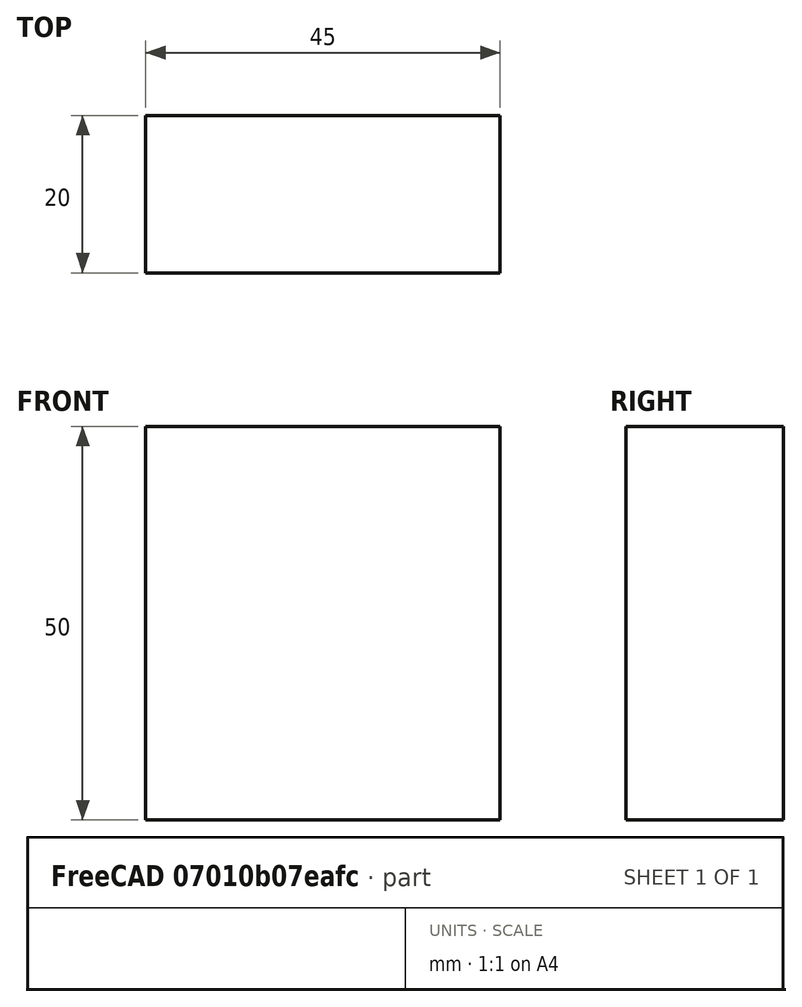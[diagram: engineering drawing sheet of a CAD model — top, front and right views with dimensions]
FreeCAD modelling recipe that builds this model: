
FCSTD DOCUMENT  (FreeCAD 0.15R4671 (Git))
Label: Flat Bar 45x20 EN10058 S235JR
License: All rights reserved
LicenseURL: http://en.wikipedia.org/wiki/All_rights_reserved
objects: Sketcher::SketchObject×1, Part::Extrusion×1
note: 2 computed .brp shape members not serialized (recipe doc carries the construction recipe); baked Part::Feature solids carry a one-line shape summary decoded from their .brp

FEATURE [Sketcher::SketchObject] Sketch
  sketch-geometry (4):
    g0: LineSegment StartX=-22.5 StartY=-10 StartZ=0 EndX=22.5 EndY=-10 EndZ=0
    g1: LineSegment StartX=22.5 StartY=-10 StartZ=0 EndX=22.5 EndY=10 EndZ=0
    g2: LineSegment StartX=22.5 StartY=10 StartZ=0 EndX=-22.5 EndY=10 EndZ=0
    g3: LineSegment StartX=-22.5 StartY=10 StartZ=0 EndX=-22.5 EndY=-10 EndZ=0
  constraints (12):
    c: Coincident(g0,g1)
    c: Coincident(g1,g2)
    c: Coincident(g2,g3)
    c: Coincident(g3,g0)
    c: Horizontal(g0)
    c: Horizontal(g2)
    c: Vertical(g1)
    c: Vertical(g3)
    c: Symmetric(g1,g2,g-2)
    c: Symmetric(g0,g1,g-1)
    c: DistanceY(g1) = 20
    c: DistanceX(g0) = 45
FEATURE [Part::Extrusion] Extrude  label="Flat Bar 45x20 EN10058 S235JR"
  Base = -> Sketch
  Dir = (0,0,50)
  Solid = true
